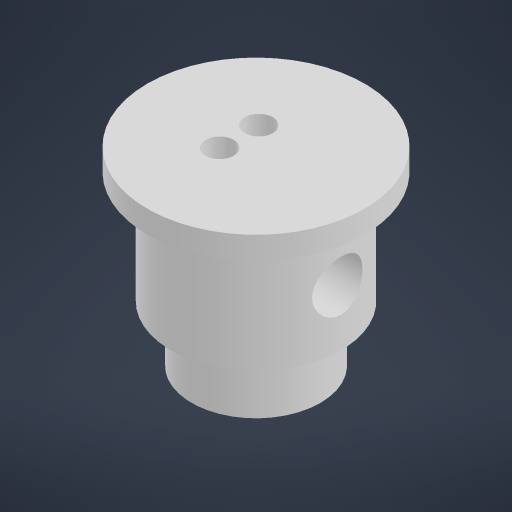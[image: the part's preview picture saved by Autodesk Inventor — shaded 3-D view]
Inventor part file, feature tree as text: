
AUTODESK INVENTOR PART (.ipt)
format: ipt  version: 2024.1 (Build 281209000, 209)  size: 196,096 bytes
history: native  units: mm
features: extrude x5, sketch x4
ambient origin geometry x8: Origin, YZ Plane, XZ Plane, XY Plane, X Axis, Y Axis, Z Axis, Center Point
bodies: Solid1 (feature_tree)
feature tree (9):
  sketch  "Sketch1"  dims[d0=15.2mm d1=19.4mm]
  extrude  "Extrusion1"  Depth=19.4mm
  extrude  "Extrusion2"  Depth=10.0mm TaperAngle=0.0deg
  extrude  "Extrusion3"  Depth=5.0mm
  extrude  "Extrusion4"  Depth=10.0mm
  sketch  "Sketch6"  dims[d8=23.0mm d9=0.0mm d10=7.5mm d11=2.0mm d12=5.0mm d13=0.0mm d18=2.5mm d19=10.0mm d20=0.0mm d24=3.5mm d25=1.5mm d21=0.5mm d22=0.872665mm d23=0.5mm]
  extrude  "Extrusion6"  Depth=2.0mm
  sketch  "Sketch2"  dims[d2=2.0mm d3=0.0mm d4=10.0mm d5=0.0mm]
  sketch  "Sketch3"  dims[d6=4.5mm d7=5.0mm]
